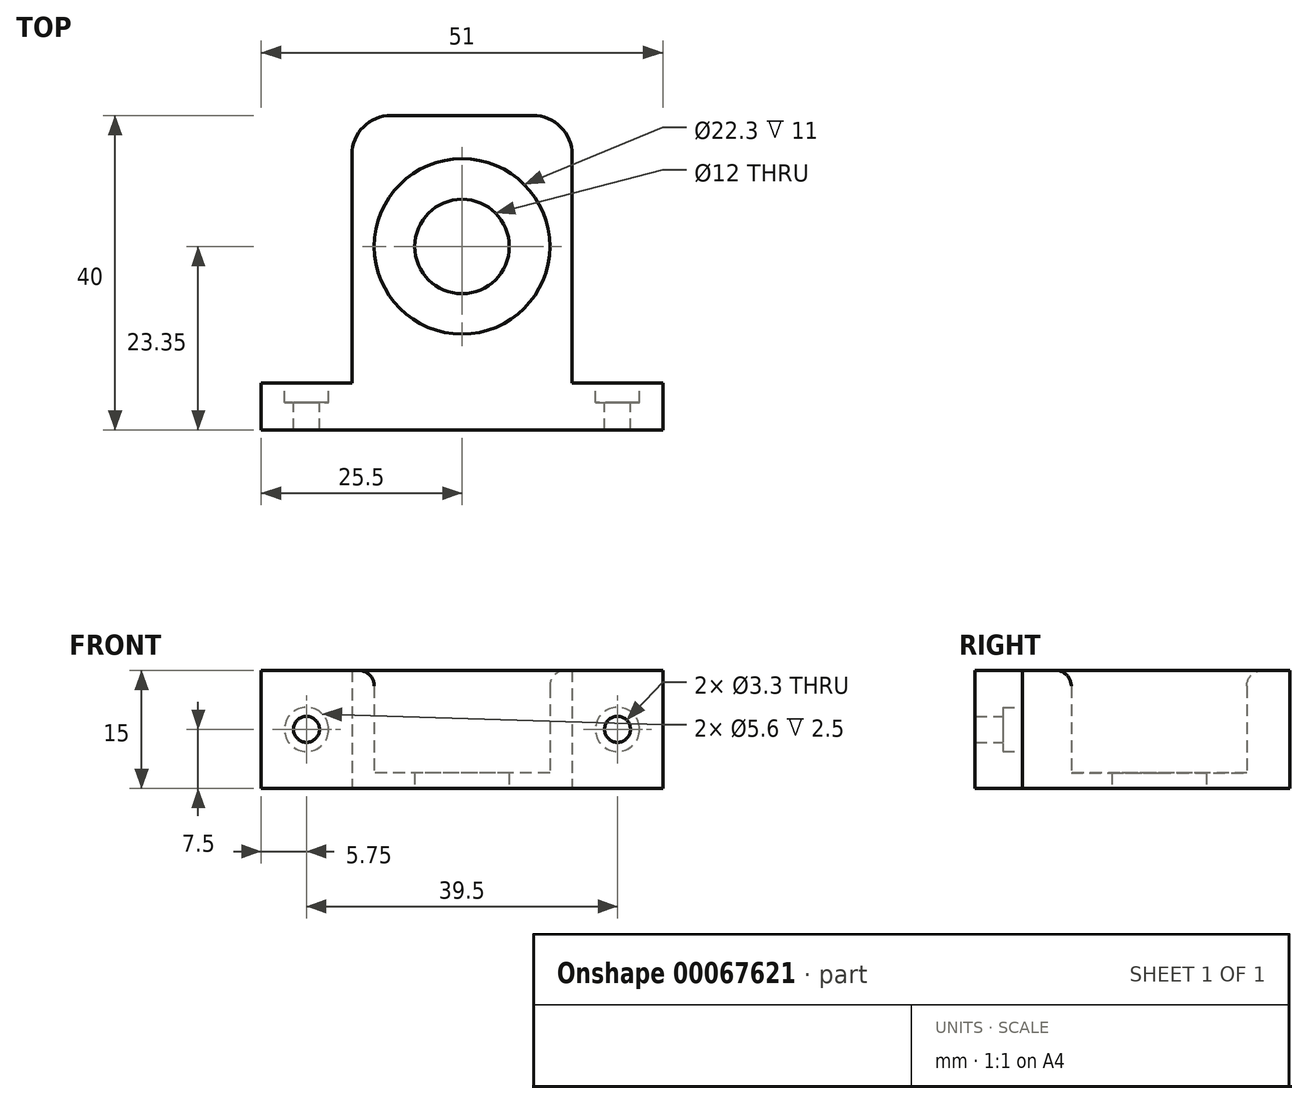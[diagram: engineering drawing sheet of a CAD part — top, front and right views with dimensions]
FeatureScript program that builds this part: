
annotation { "Feature Type Name" : "Feature", "Feature Type Description" : "" }
export const myFeature = defineFeature(function(context is Context, id is Id, definition is map)
    precondition{}
    {
        {
            var Q0;
            Q0=qCreatedBy(makeId("Top.planeOp"),FACE);
            var sketch = newSketch(context, id + "F0", { "sketchPlane" : qUnion([Q0])});
            skLineSegment(sketch, "E0.bottom", {"start": v(-14, 17) * mm, "end": v(14, 17) * mm});
            skLineSegment(sketch, "E0.top", {"start": v(-14, -17) * mm, "end": v(14, -17) * mm});
            skLineSegment(sketch, "E0.left", {"start": v(-14, 17) * mm, "end": v(-14, -17) * mm});
            skLineSegment(sketch, "E0.right", {"start": v(14, 17) * mm, "end": v(14, -17) * mm});
            skPoint(sketch, "E0.middle", {"position": v(0, 0) * mm});
            skLineSegment(sketch, "E1.bottom", {"start": v(-25.5, -17) * mm, "end": v(25.5, -17) * mm});
            skLineSegment(sketch, "E1.top", {"start": v(-25.5, -23) * mm, "end": v(25.5, -23) * mm});
            skLineSegment(sketch, "E1.left", {"start": v(-25.5, -17) * mm, "end": v(-25.5, -23) * mm});
            skLineSegment(sketch, "E1.right", {"start": v(25.5, -17) * mm, "end": v(25.5, -23) * mm});
            skCircle(sketch, "E2", {"center": v(0, 0.35) * mm, "radius": 11.15 * mm});
            skCircle(sketch, "E3", {"center": v(0, 0.35) * mm, "radius": 6 * mm});
            skSolve(sketch);
        }
        {
            var Q0;
            Q0=makeQuery(id+"F0.imprint","IMPRINT",FACE,{"disambiguationData":[TD([[makeQuery(id+"F0.imprint","IMPRINT",EDGE,{"derivedFrom":sQuery(id+"F0.wireOp",EDGE,"E0.bottom")}),-1.0]])]});
            var Q1;
            Q1=makeQuery(id+"F0.imprint","IMPRINT",FACE,{"disambiguationData":[TD([[makeQuery(id+"F0.imprint","IMPRINT",EDGE,{"derivedFrom":sQuery(id+"F0.wireOp",EDGE,"E1.top")}),1.0]])]});
            extrude(context, id + "F1", {"entities" : qUnion([Q0, Q1]), "depth" : 15 * mm});
        }
        {
            var Q0;
            Q0=makeQuery(id+"F0.imprint","IMPRINT",FACE,{"disambiguationData":[TD([[makeQuery(id+"F0.imprint","IMPRINT",EDGE,{"derivedFrom":sQuery(id+"F0.wireOp",EDGE,"E2")}),1.0]])]});
            extrude(context, id + "F2", {"entities" : qUnion([Q0]), "operationType" : NewBodyOperationType.ADD, "depth" : 2 * mm});
        }
        {
            var Q0;
            {var subQ0=sQuery(id+"F0.wireOp",EDGE,"E1.bottom");Q0=makeQuery(id+"F1.opExtrude","SWEPT_FACE",FACE,{"disambiguationData":[OSD([subQ0]),TDD([makeQuery(id+"F0.imprint","IMPRINT",EDGE,{"disambiguationData":[TD([[makeQuery(id+"F0.imprint","INTERSECT",VERTEX,{"derivedFrom":[sQuery(id+"F0.wireOp",EDGE,"E0.left"),subQ0]}),1.0]])],"derivedFrom":subQ0})])]});}
            var sketch = newSketch(context, id + "F3", { "sketchPlane" : qUnion([Q0])});
            skCircle(sketch, "E4", {"center": v(19.75, 7.5) * mm, "radius": 1.65 * mm});
            skCircle(sketch, "E5", {"center": v(19.75, 7.5) * mm, "radius": 2.8 * mm});
            skSolve(sketch);
        }
        {
            var Q0;
            Q0=makeQuery(id+"F3.imprint","IMPRINT",FACE,{"disambiguationData":[TD([[makeQuery(id+"F3.imprint","IMPRINT",EDGE,{"derivedFrom":sQuery(id+"F3.wireOp",EDGE,"E4")}),1.0]])]});
            extrude(context, id + "F4", {"entities" : qUnion([Q0]), "operationType" : NewBodyOperationType.REMOVE, "endBound" : BoundingType.UP_TO_NEXT, "oppositeDirection" : true, "depth" : 25 * mm});
        }
        {
            var Q0;
            Q0=makeQuery(id+"F3.imprint","IMPRINT",FACE,{"disambiguationData":[TD([[makeQuery(id+"F3.imprint","IMPRINT",EDGE,{"derivedFrom":sQuery(id+"F3.wireOp",EDGE,"E4")}),-1.0]])]});
            extrude(context, id + "F5", {"entities" : qUnion([Q0]), "operationType" : NewBodyOperationType.REMOVE, "oppositeDirection" : true, "depth" : 2.5 * mm});
        }
        {
            var Q0;
            Q0=makeQuery(id+"F1.opExtrude","SWEPT_BODY",BODY,{"disambiguationData":[OSD([sQuery(id+"F0.wireOp",EDGE,"E0.bottom"),sQuery(id+"F0.wireOp",EDGE,"E0.left"),sQuery(id+"F0.wireOp",EDGE,"E0.right"),sQuery(id+"F0.wireOp",EDGE,"E1.bottom"),sQuery(id+"F0.wireOp",EDGE,"E1.top"),sQuery(id+"F0.wireOp",EDGE,"E1.left"),sQuery(id+"F0.wireOp",EDGE,"E1.right"),sQuery(id+"F0.wireOp",EDGE,"E2")])]});
            var Q1;
            {var subQ0=sQuery(id+"F0.wireOp",EDGE,"E1.bottom");Q1=makeQuery(id+"F1.opExtrude","SWEPT_FACE",FACE,{"disambiguationData":[OSD([subQ0]),TDD([makeQuery(id+"F0.imprint","IMPRINT",EDGE,{"disambiguationData":[TD([[makeQuery(id+"F0.imprint","INTERSECT",VERTEX,{"derivedFrom":[sQuery(id+"F0.wireOp",EDGE,"E0.left"),subQ0]}),1.0]])],"derivedFrom":subQ0})])]});}
            var Q2;
            Q2=makeQuery(id+"F5.boolean.opBoolean","COPY",FACE,{"derivedFrom":makeQuery(id+"F5.opExtrude","CAP_FACE",FACE,{"disambiguationData":[OSD([sQuery(id+"F3.wireOp",EDGE,"E4"),sQuery(id+"F3.wireOp",EDGE,"E5")])],"isStart":false})});
            var Q3;
            Q3=qCreatedBy(makeId("Right.planeOp"),FACE);
            mirror(context, id + "F6", {"operationType" : NewBodyOperationType.INTERSECT, "entities" : qUnion([Q0]), "faces" : qUnion([Q1, Q2]), "mirrorPlane" : qUnion([Q3])});
        }
        {
            var Q0;
            Q0=makeQuery(id+"F1.opExtrude","SWEPT_EDGE",EDGE,{"disambiguationData":[OSD([sQuery(id+"F0.wireOp",EDGE,"E0.bottom"),sQuery(id+"F0.wireOp",EDGE,"E0.left")])]});
            var Q1;
            Q1=makeQuery(id+"F1.opExtrude","SWEPT_EDGE",EDGE,{"disambiguationData":[OSD([sQuery(id+"F0.wireOp",EDGE,"E0.bottom"),sQuery(id+"F0.wireOp",EDGE,"E0.right")])]});
            fillet(context, id + "F7", {"entities" : qUnion([Q0, Q1]), "radius" : 5 * mm, "tangentPropagation" : true, "allowEdgeOverflow" : false});
        }
        {
            var Q0;
            Q0=makeQuery(id+"F1.opExtrude","CAP_EDGE",EDGE,{"disambiguationData":[OSD([sQuery(id+"F0.wireOp",EDGE,"E2")])],"isStart":false});
            fillet(context, id + "F8", {"entities" : qUnion([Q0]), "radius" : 2 * mm, "tangentPropagation" : true, "allowEdgeOverflow" : false});
        }
    });
